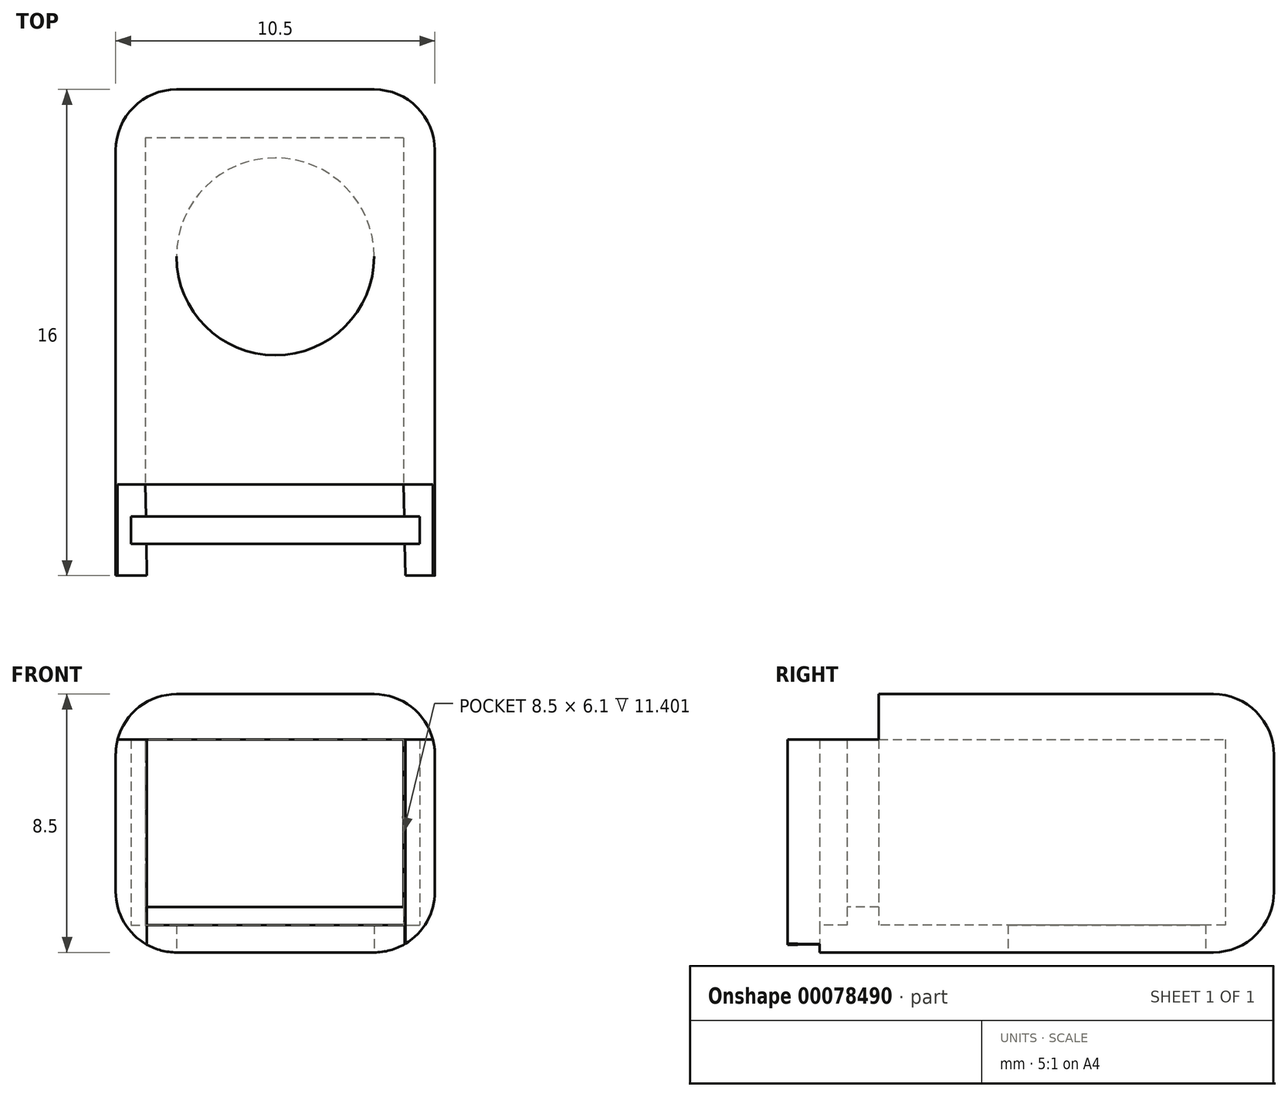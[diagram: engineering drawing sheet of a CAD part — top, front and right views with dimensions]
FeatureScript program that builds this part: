
annotation { "Feature Type Name" : "Feature", "Feature Type Description" : "" }
export const myFeature = defineFeature(function(context is Context, id is Id, definition is map)
    precondition{}
    {
        {
            var Q0;
            Q0=qCreatedBy(makeId("Top.planeOp"),FACE);
            var sketch = newSketch(context, id + "F0", { "sketchPlane" : qUnion([Q0])});
            skPoint(sketch, "E0.rect.middle", {"position": v(0, 0) * mm});
            skLineSegment(sketch, "E1.rect.bottom", {"start": v(-5.25, -1.5) * mm, "end": v(5.25, -1.5) * mm});
            skLineSegment(sketch, "E1.rect.top", {"start": v(-5.25, 1.5) * mm, "end": v(-4.28, 1.5) * mm});
            skLineSegment(sketch, "E1.rect.left", {"start": v(-5.25, -1.5) * mm, "end": v(-5.25, 1.5) * mm});
            skLineSegment(sketch, "E1.rect.right", {"start": v(5.25, -1.5) * mm, "end": v(5.25, 1.5) * mm});
            skLineSegment(sketch, "E2.rect.bottom", {"start": v(4.75, -0.45) * mm, "end": v(-4.75, -0.45) * mm});
            skLineSegment(sketch, "E2.rect.top", {"start": v(4.75, 0.45) * mm, "end": v(-4.75, 0.45) * mm});
            skLineSegment(sketch, "E2.rect.left", {"start": v(4.75, -0.45) * mm, "end": v(4.75, 0.45) * mm});
            skLineSegment(sketch, "E2.rect.right", {"start": v(-4.75, -0.45) * mm, "end": v(-4.75, 0.45) * mm});
            skLineSegment(sketch, "E3.rect.bottom", {"start": v(-4.22, -1.5) * mm, "end": v(4.28, -1.5) * mm});
            skLineSegment(sketch, "E3.rect.left", {"start": v(-4.22, -1.5) * mm, "end": v(-4.28, 1.5) * mm});
            skLineSegment(sketch, "E3.rect.right", {"start": v(4.28, -1.5) * mm, "end": v(4.22, 1.5) * mm});
            skLineSegment(sketch, "E4.trimOffspring", {"start": v(4.22, 1.5) * mm, "end": v(5.25, 1.5) * mm});
            skLineSegment(sketch, "E5", {"start": v(-4.28, 1.5) * mm, "end": v(4.22, 1.5) * mm, "construction": true});
            skLineSegment(sketch, "E6.bottom", {"start": v(5.25, 1.5) * mm, "end": v(-5.25, 1.5) * mm});
            skLineSegment(sketch, "E7.bottom", {"start": v(4.22, 1.5) * mm, "end": v(-5.25, 1.5) * mm});
            skLineSegment(sketch, "E8.bottom", {"start": v(-5.25, 1.5) * mm, "end": v(5.25, 1.5) * mm});
            skLineSegment(sketch, "E8.top", {"start": v(-5.25, 14.5) * mm, "end": v(5.25, 14.5) * mm});
            skLineSegment(sketch, "E8.left", {"start": v(-5.25, 1.5) * mm, "end": v(-5.25, 14.5) * mm});
            skLineSegment(sketch, "E8.right", {"start": v(5.25, 1.5) * mm, "end": v(5.25, 14.5) * mm});
            skLineSegment(sketch, "E9", {"start": v(-4.28, 1.5) * mm, "end": v(-4.28, 14.5) * mm});
            skLineSegment(sketch, "E10", {"start": v(4.22, 1.5) * mm, "end": v(4.22, 14.5) * mm});
            skLineSegment(sketch, "E11", {"start": v(-5.25, 12.9) * mm, "end": v(5.25, 12.9) * mm});
            skSolve(sketch);
        }
        {
            var Q0;
            {var subQ0=sQuery(id+"F0.wireOp",EDGE,"E6.right");Q0=makeQuery(id+"F0.imprint","IMPRINT",FACE,{"disambiguationData":[TD([[makeQuery(id+"F0.imprint","IMPRINT",EDGE,{"derivedFrom":subQ0}),-1.0]])]});}
            var Q1;
            Q1=makeQuery(id+"F0.imprint","IMPRINT",FACE,{"disambiguationData":[TD([[makeQuery(id+"F0.imprint","IMPRINT",EDGE,{"derivedFrom":sQuery(id+"F0.wireOp",EDGE,"E7.bottom")}),-1.0]])]});
            var Q2;
            {var subQ5=sQuery(id+"F0.wireOp",EDGE,"E7.bottom");Q2=makeQuery(id+"F0.imprint","IMPRINT",FACE,{"disambiguationData":[TD([[makeQuery(id+"F0.imprint","IMPRINT",EDGE,{"derivedFrom":subQ5}),1.0]])]});}
            var Q3;
            {var subQ8=sQuery(id+"F0.wireOp",EDGE,"E1.rect.right");Q3=makeQuery(id+"F0.imprint","IMPRINT",FACE,{"disambiguationData":[TD([[makeQuery(id+"F0.imprint","IMPRINT",EDGE,{"derivedFrom":subQ8}),1.0]])]});}
            var Q4;
            {var subQ5=sQuery(id+"F0.wireOp",EDGE,"E3.rect.bottom");Q4=makeQuery(id+"F0.imprint","IMPRINT",FACE,{"disambiguationData":[TD([[makeQuery(id+"F0.imprint","IMPRINT",EDGE,{"derivedFrom":subQ5}),1.0]])]});}
            var Q5;
            {var subQ4=sQuery(id+"F0.wireOp",EDGE,"E1.rect.left");Q5=makeQuery(id+"F0.imprint","IMPRINT",FACE,{"disambiguationData":[TD([[makeQuery(id+"F0.imprint","IMPRINT",EDGE,{"derivedFrom":subQ4}),-1.0]])]});}
            var Q6;
            {var subQ0=sQuery(id+"F0.wireOp",EDGE,"E6.left");Q6=makeQuery(id+"F0.imprint","IMPRINT",FACE,{"disambiguationData":[TD([[makeQuery(id+"F0.imprint","IMPRINT",EDGE,{"derivedFrom":subQ0}),1.0]])]});}
            var Q7;
            {var subQ0=sQuery(id+"F0.wireOp",EDGE,"E3.rect.right");var subQ1=sQuery(id+"F0.wireOp",EDGE,"E2.rect.bottom");var subQ2=makeQuery(id+"F0.imprint","INTERSECT",VERTEX,{"derivedFrom":[subQ1,subQ0]});Q7=makeQuery(id+"F0.imprint","IMPRINT",FACE,{"disambiguationData":[TD([[makeQuery(id+"F0.imprint","IMPRINT",EDGE,{"disambiguationData":[TD([[subQ2,-1.0]])],"derivedFrom":subQ1}),-1.0]])]});}
            var Q8;
            {var subQ0=sQuery(id+"F0.wireOp",EDGE,"E2.rect.right");Q8=makeQuery(id+"F0.imprint","IMPRINT",FACE,{"disambiguationData":[TD([[makeQuery(id+"F0.imprint","IMPRINT",EDGE,{"derivedFrom":subQ0}),-1.0]])]});}
            var Q9;
            {var subQ0=sQuery(id+"F0.wireOp",EDGE,"E2.rect.left");Q9=makeQuery(id+"F0.imprint","IMPRINT",FACE,{"disambiguationData":[TD([[makeQuery(id+"F0.imprint","IMPRINT",EDGE,{"derivedFrom":subQ0}),1.0]])]});}
            var Q10;
            {var subQ0=sQuery(id+"F0.wireOp",EDGE,"E8.left");var subQ5=sQuery(id+"F0.wireOp",EDGE,"GkOf4P8d-EZpd-A0Uh-Zg2V-Pxibx59UNKdc");var subQ6=makeQuery(id+"F0.imprint","INTERSECT",VERTEX,{"derivedFrom":[subQ0,subQ5]});Q10=makeQuery(id+"F0.imprint","IMPRINT",FACE,{"disambiguationData":[TD([[makeQuery(id+"F0.imprint","IMPRINT",EDGE,{"disambiguationData":[TD([[subQ6,1.0]])],"derivedFrom":subQ5}),1.0]])]});}
            var Q11;
            {var subQ0=sQuery(id+"F0.wireOp",EDGE,"E8.left");var subQ1=sQuery(id+"F0.wireOp",EDGE,"E8.top");var subQ2=makeQuery(id+"F0.imprint","INTERSECT",VERTEX,{"derivedFrom":[subQ1,subQ0]});Q11=makeQuery(id+"F0.imprint","IMPRINT",FACE,{"disambiguationData":[TD([[makeQuery(id+"F0.imprint","IMPRINT",EDGE,{"disambiguationData":[TD([[subQ2,-1.0]])],"derivedFrom":subQ1}),-1.0]])]});}
            var Q12;
            {var subQ0=sQuery(id+"F0.wireOp",EDGE,"E9");var subQ1=sQuery(id+"F0.wireOp",EDGE,"E8.top");var subQ2=makeQuery(id+"F0.imprint","INTERSECT",VERTEX,{"derivedFrom":[subQ1,subQ0]});Q12=makeQuery(id+"F0.imprint","IMPRINT",FACE,{"disambiguationData":[TD([[makeQuery(id+"F0.imprint","IMPRINT",EDGE,{"disambiguationData":[TD([[subQ2,-1.0]])],"derivedFrom":subQ1}),-1.0]])]});}
            var Q13;
            {var subQ0=sQuery(id+"F0.wireOp",EDGE,"E8.right");var subQ1=sQuery(id+"F0.wireOp",EDGE,"E8.top");var subQ2=makeQuery(id+"F0.imprint","INTERSECT",VERTEX,{"derivedFrom":[subQ1,subQ0]});Q13=makeQuery(id+"F0.imprint","IMPRINT",FACE,{"disambiguationData":[TD([[makeQuery(id+"F0.imprint","IMPRINT",EDGE,{"disambiguationData":[TD([[subQ2,1.0]])],"derivedFrom":subQ1}),-1.0]])]});}
            var Q14;
            {var subQ0=sQuery(id+"F0.wireOp",EDGE,"E8.right");var subQ5=sQuery(id+"F0.wireOp",EDGE,"GkOf4P8d-EZpd-A0Uh-Zg2V-Pxibx59UNKdc");var subQ6=makeQuery(id+"F0.imprint","INTERSECT",VERTEX,{"derivedFrom":[subQ0,subQ5]});Q14=makeQuery(id+"F0.imprint","IMPRINT",FACE,{"disambiguationData":[TD([[makeQuery(id+"F0.imprint","IMPRINT",EDGE,{"disambiguationData":[TD([[subQ6,-1.0]])],"derivedFrom":subQ5}),1.0]])]});}
            var Q15;
            {var subQ0=sQuery(id+"F0.wireOp",EDGE,"E3.rect.right");var subQ1=sQuery(id+"F0.wireOp",EDGE,"E2.rect.top");var subQ2=makeQuery(id+"F0.imprint","INTERSECT",VERTEX,{"derivedFrom":[subQ1,subQ0]});Q15=makeQuery(id+"F0.imprint","IMPRINT",FACE,{"disambiguationData":[TD([[makeQuery(id+"F0.imprint","IMPRINT",EDGE,{"disambiguationData":[TD([[subQ2,-1.0]])],"derivedFrom":subQ1}),-1.0]])]});}
            var Q16;
            {var subQ0=sQuery(id+"F0.wireOp",EDGE,"E9");var subQ5=sQuery(id+"F0.wireOp",EDGE,"GkOf4P8d-EZpd-A0Uh-Zg2V-Pxibx59UNKdc");var subQ6=makeQuery(id+"F0.imprint","INTERSECT",VERTEX,{"derivedFrom":[subQ0,subQ5]});Q16=makeQuery(id+"F0.imprint","IMPRINT",FACE,{"disambiguationData":[TD([[makeQuery(id+"F0.imprint","IMPRINT",EDGE,{"disambiguationData":[TD([[subQ6,1.0]])],"derivedFrom":subQ5}),1.0]])]});}
            var Q17;
            {var subQ0=sQuery(id+"F0.wireOp",EDGE,"E8.left");var subQ5=sQuery(id+"F0.wireOp",EDGE,"E11");var subQ6=makeQuery(id+"F0.imprint","INTERSECT",VERTEX,{"derivedFrom":[subQ0,subQ5]});Q17=makeQuery(id+"F0.imprint","IMPRINT",FACE,{"disambiguationData":[TD([[makeQuery(id+"F0.imprint","IMPRINT",EDGE,{"disambiguationData":[TD([[subQ6,-1.0]])],"derivedFrom":subQ5}),-1.0]])]});}
            var Q18;
            {var subQ0=sQuery(id+"F0.wireOp",EDGE,"E9");var subQ5=sQuery(id+"F0.wireOp",EDGE,"E11");var subQ6=makeQuery(id+"F0.imprint","INTERSECT",VERTEX,{"derivedFrom":[subQ0,subQ5]});Q18=makeQuery(id+"F0.imprint","IMPRINT",FACE,{"disambiguationData":[TD([[makeQuery(id+"F0.imprint","IMPRINT",EDGE,{"disambiguationData":[TD([[subQ6,-1.0]])],"derivedFrom":subQ5}),-1.0]])]});}
            var Q19;
            {var subQ0=sQuery(id+"F0.wireOp",EDGE,"E8.right");var subQ5=sQuery(id+"F0.wireOp",EDGE,"E11");var subQ6=makeQuery(id+"F0.imprint","INTERSECT",VERTEX,{"derivedFrom":[subQ0,subQ5]});Q19=makeQuery(id+"F0.imprint","IMPRINT",FACE,{"disambiguationData":[TD([[makeQuery(id+"F0.imprint","IMPRINT",EDGE,{"disambiguationData":[TD([[subQ6,1.0]])],"derivedFrom":subQ5}),-1.0]])]});}
            extrude(context, id + "F1", {"entities" : qUnion([Q0, Q1, Q2, Q3, Q4, Q5, Q6, Q7, Q8, Q9, Q10, Q11, Q12, Q13, Q14, Q15, Q16, Q17, Q18, Q19]), "depth" : 0.9 * mm});
        }
        {
            var Q0;
            {var subQ0=sQuery(id+"F0.wireOp",EDGE,"E6.left");Q0=makeQuery(id+"F0.imprint","IMPRINT",FACE,{"disambiguationData":[TD([[makeQuery(id+"F0.imprint","IMPRINT",EDGE,{"derivedFrom":subQ0}),1.0]])]});}
            var Q1;
            {var subQ0=sQuery(id+"F0.wireOp",EDGE,"E6.right");Q1=makeQuery(id+"F0.imprint","IMPRINT",FACE,{"disambiguationData":[TD([[makeQuery(id+"F0.imprint","IMPRINT",EDGE,{"derivedFrom":subQ0}),-1.0]])]});}
            var Q2;
            {var subQ5=sQuery(id+"F0.wireOp",EDGE,"E3.rect.bottom");Q2=makeQuery(id+"F0.imprint","IMPRINT",FACE,{"disambiguationData":[TD([[makeQuery(id+"F0.imprint","IMPRINT",EDGE,{"derivedFrom":subQ5}),1.0]])]});}
            var Q3;
            {var subQ4=sQuery(id+"F0.wireOp",EDGE,"E1.rect.left");Q3=makeQuery(id+"F0.imprint","IMPRINT",FACE,{"disambiguationData":[TD([[makeQuery(id+"F0.imprint","IMPRINT",EDGE,{"derivedFrom":subQ4}),-1.0]])]});}
            var Q4;
            {var subQ8=sQuery(id+"F0.wireOp",EDGE,"E1.rect.right");Q4=makeQuery(id+"F0.imprint","IMPRINT",FACE,{"disambiguationData":[TD([[makeQuery(id+"F0.imprint","IMPRINT",EDGE,{"derivedFrom":subQ8}),1.0]])]});}
            var Q5;
            {var subQ5=sQuery(id+"F0.wireOp",EDGE,"E7.bottom");Q5=makeQuery(id+"F0.imprint","IMPRINT",FACE,{"disambiguationData":[TD([[makeQuery(id+"F0.imprint","IMPRINT",EDGE,{"derivedFrom":subQ5}),1.0]])]});}
            var Q6;
            {var subQ0=sQuery(id+"F0.wireOp",EDGE,"E8.right");var subQ5=sQuery(id+"F0.wireOp",EDGE,"GkOf4P8d-EZpd-A0Uh-Zg2V-Pxibx59UNKdc");var subQ6=makeQuery(id+"F0.imprint","INTERSECT",VERTEX,{"derivedFrom":[subQ0,subQ5]});Q6=makeQuery(id+"F0.imprint","IMPRINT",FACE,{"disambiguationData":[TD([[makeQuery(id+"F0.imprint","IMPRINT",EDGE,{"disambiguationData":[TD([[subQ6,-1.0]])],"derivedFrom":subQ5}),1.0]])]});}
            var Q7;
            {var subQ0=sQuery(id+"F0.wireOp",EDGE,"E3.rect.right");var subQ1=sQuery(id+"F0.wireOp",EDGE,"E2.rect.top");var subQ2=makeQuery(id+"F0.imprint","INTERSECT",VERTEX,{"derivedFrom":[subQ1,subQ0]});Q7=makeQuery(id+"F0.imprint","IMPRINT",FACE,{"disambiguationData":[TD([[makeQuery(id+"F0.imprint","IMPRINT",EDGE,{"disambiguationData":[TD([[subQ2,-1.0]])],"derivedFrom":subQ1}),-1.0]])]});}
            var Q8;
            {var subQ0=sQuery(id+"F0.wireOp",EDGE,"E9");var subQ5=sQuery(id+"F0.wireOp",EDGE,"GkOf4P8d-EZpd-A0Uh-Zg2V-Pxibx59UNKdc");var subQ6=makeQuery(id+"F0.imprint","INTERSECT",VERTEX,{"derivedFrom":[subQ0,subQ5]});Q8=makeQuery(id+"F0.imprint","IMPRINT",FACE,{"disambiguationData":[TD([[makeQuery(id+"F0.imprint","IMPRINT",EDGE,{"disambiguationData":[TD([[subQ6,1.0]])],"derivedFrom":subQ5}),1.0]])]});}
            var Q9;
            {var subQ0=sQuery(id+"F0.wireOp",EDGE,"E8.left");var subQ5=sQuery(id+"F0.wireOp",EDGE,"GkOf4P8d-EZpd-A0Uh-Zg2V-Pxibx59UNKdc");var subQ6=makeQuery(id+"F0.imprint","INTERSECT",VERTEX,{"derivedFrom":[subQ0,subQ5]});Q9=makeQuery(id+"F0.imprint","IMPRINT",FACE,{"disambiguationData":[TD([[makeQuery(id+"F0.imprint","IMPRINT",EDGE,{"disambiguationData":[TD([[subQ6,1.0]])],"derivedFrom":subQ5}),1.0]])]});}
            var Q10;
            {var subQ0=sQuery(id+"F0.wireOp",EDGE,"E8.left");var subQ1=sQuery(id+"F0.wireOp",EDGE,"E8.top");var subQ2=makeQuery(id+"F0.imprint","INTERSECT",VERTEX,{"derivedFrom":[subQ1,subQ0]});Q10=makeQuery(id+"F0.imprint","IMPRINT",FACE,{"disambiguationData":[TD([[makeQuery(id+"F0.imprint","IMPRINT",EDGE,{"disambiguationData":[TD([[subQ2,-1.0]])],"derivedFrom":subQ1}),-1.0]])]});}
            var Q11;
            {var subQ0=sQuery(id+"F0.wireOp",EDGE,"E9");var subQ1=sQuery(id+"F0.wireOp",EDGE,"E8.top");var subQ2=makeQuery(id+"F0.imprint","INTERSECT",VERTEX,{"derivedFrom":[subQ1,subQ0]});Q11=makeQuery(id+"F0.imprint","IMPRINT",FACE,{"disambiguationData":[TD([[makeQuery(id+"F0.imprint","IMPRINT",EDGE,{"disambiguationData":[TD([[subQ2,-1.0]])],"derivedFrom":subQ1}),-1.0]])]});}
            var Q12;
            {var subQ0=sQuery(id+"F0.wireOp",EDGE,"E8.right");var subQ1=sQuery(id+"F0.wireOp",EDGE,"E8.top");var subQ2=makeQuery(id+"F0.imprint","INTERSECT",VERTEX,{"derivedFrom":[subQ1,subQ0]});Q12=makeQuery(id+"F0.imprint","IMPRINT",FACE,{"disambiguationData":[TD([[makeQuery(id+"F0.imprint","IMPRINT",EDGE,{"disambiguationData":[TD([[subQ2,1.0]])],"derivedFrom":subQ1}),-1.0]])]});}
            var Q13;
            {var subQ0=sQuery(id+"F0.wireOp",EDGE,"E8.left");var subQ5=sQuery(id+"F0.wireOp",EDGE,"E11");var subQ6=makeQuery(id+"F0.imprint","INTERSECT",VERTEX,{"derivedFrom":[subQ0,subQ5]});Q13=makeQuery(id+"F0.imprint","IMPRINT",FACE,{"disambiguationData":[TD([[makeQuery(id+"F0.imprint","IMPRINT",EDGE,{"disambiguationData":[TD([[subQ6,-1.0]])],"derivedFrom":subQ5}),-1.0]])]});}
            var Q14;
            {var subQ0=sQuery(id+"F0.wireOp",EDGE,"E8.right");var subQ5=sQuery(id+"F0.wireOp",EDGE,"E11");var subQ6=makeQuery(id+"F0.imprint","INTERSECT",VERTEX,{"derivedFrom":[subQ0,subQ5]});Q14=makeQuery(id+"F0.imprint","IMPRINT",FACE,{"disambiguationData":[TD([[makeQuery(id+"F0.imprint","IMPRINT",EDGE,{"disambiguationData":[TD([[subQ6,1.0]])],"derivedFrom":subQ5}),-1.0]])]});}
            extrude(context, id + "F2", {"entities" : qUnion([Q0, Q1, Q2, Q3, Q4, Q5, Q6, Q7, Q8, Q9, Q10, Q11, Q12, Q13, Q14]), "operationType" : NewBodyOperationType.ADD, "depth" : 1.5 * mm});
        }
        {
            var Q0;
            {var subQ9=sQuery(id+"F0.wireOp",EDGE,"E1.rect.top");Q0=makeQuery(id+"F0.imprint","IMPRINT",FACE,{"disambiguationData":[TD([[makeQuery(id+"F0.imprint","IMPRINT",EDGE,{"derivedFrom":subQ9}),-1.0]])]});}
            var Q1;
            {var subQ4=sQuery(id+"F0.wireOp",EDGE,"E1.rect.right");Q1=makeQuery(id+"F0.imprint","IMPRINT",FACE,{"disambiguationData":[TD([[makeQuery(id+"F0.imprint","IMPRINT",EDGE,{"derivedFrom":subQ4}),1.0]])]});}
            var Q2;
            {var subQ4=sQuery(id+"F0.wireOp",EDGE,"E1.rect.left");Q2=makeQuery(id+"F0.imprint","IMPRINT",FACE,{"disambiguationData":[TD([[makeQuery(id+"F0.imprint","IMPRINT",EDGE,{"derivedFrom":subQ4}),-1.0]])]});}
            var Q3;
            {var subQ0=sQuery(id+"F0.wireOp",EDGE,"E6.right");Q3=makeQuery(id+"F0.imprint","IMPRINT",FACE,{"disambiguationData":[TD([[makeQuery(id+"F0.imprint","IMPRINT",EDGE,{"derivedFrom":subQ0}),-1.0]])]});}
            var Q4;
            {var subQ0=sQuery(id+"F0.wireOp",EDGE,"E6.left");Q4=makeQuery(id+"F0.imprint","IMPRINT",FACE,{"disambiguationData":[TD([[makeQuery(id+"F0.imprint","IMPRINT",EDGE,{"derivedFrom":subQ0}),1.0]])]});}
            var Q5;
            {var subQ0=sQuery(id+"F0.wireOp",EDGE,"E8.left");var subQ5=sQuery(id+"F0.wireOp",EDGE,"GkOf4P8d-EZpd-A0Uh-Zg2V-Pxibx59UNKdc");var subQ6=makeQuery(id+"F0.imprint","INTERSECT",VERTEX,{"derivedFrom":[subQ0,subQ5]});Q5=makeQuery(id+"F0.imprint","IMPRINT",FACE,{"disambiguationData":[TD([[makeQuery(id+"F0.imprint","IMPRINT",EDGE,{"disambiguationData":[TD([[subQ6,1.0]])],"derivedFrom":subQ5}),1.0]])]});}
            var Q6;
            {var subQ0=sQuery(id+"F0.wireOp",EDGE,"E8.right");var subQ5=sQuery(id+"F0.wireOp",EDGE,"GkOf4P8d-EZpd-A0Uh-Zg2V-Pxibx59UNKdc");var subQ6=makeQuery(id+"F0.imprint","INTERSECT",VERTEX,{"derivedFrom":[subQ0,subQ5]});Q6=makeQuery(id+"F0.imprint","IMPRINT",FACE,{"disambiguationData":[TD([[makeQuery(id+"F0.imprint","IMPRINT",EDGE,{"disambiguationData":[TD([[subQ6,-1.0]])],"derivedFrom":subQ5}),1.0]])]});}
            var Q7;
            {var subQ0=sQuery(id+"F0.wireOp",EDGE,"E8.left");var subQ1=sQuery(id+"F0.wireOp",EDGE,"E8.top");var subQ2=makeQuery(id+"F0.imprint","INTERSECT",VERTEX,{"derivedFrom":[subQ1,subQ0]});Q7=makeQuery(id+"F0.imprint","IMPRINT",FACE,{"disambiguationData":[TD([[makeQuery(id+"F0.imprint","IMPRINT",EDGE,{"disambiguationData":[TD([[subQ2,-1.0]])],"derivedFrom":subQ1}),-1.0]])]});}
            var Q8;
            {var subQ0=sQuery(id+"F0.wireOp",EDGE,"E9");var subQ1=sQuery(id+"F0.wireOp",EDGE,"E8.top");var subQ2=makeQuery(id+"F0.imprint","INTERSECT",VERTEX,{"derivedFrom":[subQ1,subQ0]});Q8=makeQuery(id+"F0.imprint","IMPRINT",FACE,{"disambiguationData":[TD([[makeQuery(id+"F0.imprint","IMPRINT",EDGE,{"disambiguationData":[TD([[subQ2,-1.0]])],"derivedFrom":subQ1}),-1.0]])]});}
            var Q9;
            {var subQ0=sQuery(id+"F0.wireOp",EDGE,"E8.right");var subQ1=sQuery(id+"F0.wireOp",EDGE,"E8.top");var subQ2=makeQuery(id+"F0.imprint","INTERSECT",VERTEX,{"derivedFrom":[subQ1,subQ0]});Q9=makeQuery(id+"F0.imprint","IMPRINT",FACE,{"disambiguationData":[TD([[makeQuery(id+"F0.imprint","IMPRINT",EDGE,{"disambiguationData":[TD([[subQ2,1.0]])],"derivedFrom":subQ1}),-1.0]])]});}
            var Q10;
            {var subQ0=sQuery(id+"F0.wireOp",EDGE,"E8.left");var subQ5=sQuery(id+"F0.wireOp",EDGE,"E11");var subQ6=makeQuery(id+"F0.imprint","INTERSECT",VERTEX,{"derivedFrom":[subQ0,subQ5]});Q10=makeQuery(id+"F0.imprint","IMPRINT",FACE,{"disambiguationData":[TD([[makeQuery(id+"F0.imprint","IMPRINT",EDGE,{"disambiguationData":[TD([[subQ6,-1.0]])],"derivedFrom":subQ5}),-1.0]])]});}
            var Q11;
            {var subQ0=sQuery(id+"F0.wireOp",EDGE,"E8.right");var subQ5=sQuery(id+"F0.wireOp",EDGE,"E11");var subQ6=makeQuery(id+"F0.imprint","INTERSECT",VERTEX,{"derivedFrom":[subQ0,subQ5]});Q11=makeQuery(id+"F0.imprint","IMPRINT",FACE,{"disambiguationData":[TD([[makeQuery(id+"F0.imprint","IMPRINT",EDGE,{"disambiguationData":[TD([[subQ6,1.0]])],"derivedFrom":subQ5}),-1.0]])]});}
            extrude(context, id + "F3", {"entities" : qUnion([Q0, Q1, Q2, Q3, Q4, Q5, Q6, Q7, Q8, Q9, Q10, Q11]), "operationType" : NewBodyOperationType.ADD, "depth" : 7 * mm});
        }
        {
            var Q0;
            Q0=makeQuery(id+"F3.opExtrude","CAP_FACE",FACE,{"disambiguationData":[OSD([sQuery(id+"F0.wireOp",EDGE,"E1.rect.bottom"),sQuery(id+"F0.wireOp",EDGE,"E1.rect.left"),sQuery(id+"F0.wireOp",EDGE,"E1.rect.right"),sQuery(id+"F0.wireOp",EDGE,"E2.rect.bottom"),sQuery(id+"F0.wireOp",EDGE,"E2.rect.top"),sQuery(id+"F0.wireOp",EDGE,"E2.rect.left"),sQuery(id+"F0.wireOp",EDGE,"E2.rect.right"),sQuery(id+"F0.wireOp",EDGE,"E3.rect.left"),sQuery(id+"F0.wireOp",EDGE,"E3.rect.right"),sQuery(id+"F0.wireOp",EDGE,"E8.top"),sQuery(id+"F0.wireOp",EDGE,"E8.left"),sQuery(id+"F0.wireOp",EDGE,"E8.right"),sQuery(id+"F0.wireOp",EDGE,"E9"),sQuery(id+"F0.wireOp",EDGE,"E10"),sQuery(id+"F0.wireOp",EDGE,"GkOf4P8d-EZpd-A0Uh-Zg2V-Pxibx59UNKdc")])],"isStart":false});
            cPlane(context, id + "F4", {"entities" : qUnion([Q0]), "cplaneType" : CPlaneType.OFFSET, "offset" : 0 * mm, "width" : 150 * mm, "height" : 150 * mm});
        }
        {
            var Q0;
            Q0=qCreatedBy(id+"F4.planeOp",FACE);
            var sketch = newSketch(context, id + "F5", { "sketchPlane" : qUnion([Q0])});
            skLineSegment(sketch, "E12.bottom", {"start": v(5.25, 1.5) * mm, "end": v(-5.25, 1.5) * mm});
            skLineSegment(sketch, "E12.top", {"start": v(5.25, -1.5) * mm, "end": v(-5.25, -1.5) * mm});
            skLineSegment(sketch, "E12.left", {"start": v(5.25, 1.5) * mm, "end": v(5.25, -1.5) * mm});
            skLineSegment(sketch, "E12.right", {"start": v(-5.25, 1.5) * mm, "end": v(-5.25, -1.5) * mm});
            skPoint(sketch, "E12.middle", {"position": v(0, 0) * mm});
            skLineSegment(sketch, "E13.top", {"start": v(5.25, 14.5) * mm, "end": v(-5.25, 14.5) * mm});
            skLineSegment(sketch, "E13.left", {"start": v(5.25, 1.5) * mm, "end": v(5.25, 14.5) * mm});
            skLineSegment(sketch, "E13.right", {"start": v(-5.25, 1.5) * mm, "end": v(-5.25, 14.5) * mm});
            skSolve(sketch);
        }
        {
            var Q0;
            Q0=makeQuery(id+"F5.imprint","IMPRINT",FACE,{"disambiguationData":[TD([[makeQuery(id+"F5.imprint","IMPRINT",EDGE,{"derivedFrom":sQuery(id+"F5.wireOp",EDGE,"E12.bottom")}),-1.0]])]});
            extrude(context, id + "F6", {"entities" : qUnion([Q0]), "operationType" : NewBodyOperationType.ADD, "depth" : 1.5 * mm});
        }
        {
            var Q0;
            {var subQ0=sQuery(id+"F0.wireOp",EDGE,"E8.right");var subQ1=sQuery(id+"F0.wireOp",EDGE,"E8.top");Q0=makeQuery(id+"F6.boolean.opBoolean","MERGE",EDGE,{"derivedFrom":[makeQuery(id+"F3.boolean.opBoolean","MERGE",EDGE,{"derivedFrom":[makeQuery(id+"F2.boolean.opBoolean","MERGE",EDGE,{"derivedFrom":[makeQuery(id+"F1.opExtrude","SWEPT_EDGE",EDGE,{"disambiguationData":[OSD([subQ1,subQ0])]}),makeQuery(id+"F2.opExtrude","SWEPT_EDGE",EDGE,{"disambiguationData":[OSD([subQ1,subQ0])]})]}),makeQuery(id+"F3.opExtrude","SWEPT_EDGE",EDGE,{"disambiguationData":[OSD([subQ1,subQ0])]})]}),makeQuery(id+"F6.opExtrude","SWEPT_EDGE",EDGE,{"disambiguationData":[OSD([sQuery(id+"F5.wireOp",EDGE,"E13.top"),sQuery(id+"F5.wireOp",EDGE,"E13.left")])]})]});}
            var Q1;
            Q1=makeQuery(id+"F6.opExtrude","CAP_EDGE",EDGE,{"disambiguationData":[OSD([sQuery(id+"F5.wireOp",EDGE,"E13.top")])],"isStart":false});
            var Q2;
            Q2=makeQuery(id+"F6.opExtrude","CAP_EDGE",EDGE,{"disambiguationData":[OSD([sQuery(id+"F5.wireOp",EDGE,"E13.left")])],"isStart":false});
            var Q3;
            Q3=makeQuery(id+"F1.opExtrude","CAP_EDGE",EDGE,{"disambiguationData":[OSD([sQuery(id+"F0.wireOp",EDGE,"E1.rect.right"),sQuery(id+"F0.wireOp",EDGE,"E8.right")])],"isStart":true});
            var Q4;
            Q4=makeQuery(id+"F1.opExtrude","CAP_EDGE",EDGE,{"disambiguationData":[OSD([sQuery(id+"F0.wireOp",EDGE,"E8.top")])],"isStart":true});
            var Q5;
            Q5=makeQuery(id+"F1.opExtrude","CAP_EDGE",EDGE,{"disambiguationData":[OSD([sQuery(id+"F0.wireOp",EDGE,"E1.rect.left"),sQuery(id+"F0.wireOp",EDGE,"E8.left")])],"isStart":true});
            var Q6;
            {var subQ0=sQuery(id+"F0.wireOp",EDGE,"E8.left");var subQ1=sQuery(id+"F0.wireOp",EDGE,"E8.top");Q6=makeQuery(id+"F6.boolean.opBoolean","MERGE",EDGE,{"derivedFrom":[makeQuery(id+"F3.boolean.opBoolean","MERGE",EDGE,{"derivedFrom":[makeQuery(id+"F2.boolean.opBoolean","MERGE",EDGE,{"derivedFrom":[makeQuery(id+"F1.opExtrude","SWEPT_EDGE",EDGE,{"disambiguationData":[OSD([subQ1,subQ0])]}),makeQuery(id+"F2.opExtrude","SWEPT_EDGE",EDGE,{"disambiguationData":[OSD([subQ1,subQ0])]})]}),makeQuery(id+"F3.opExtrude","SWEPT_EDGE",EDGE,{"disambiguationData":[OSD([subQ1,subQ0])]})]}),makeQuery(id+"F6.opExtrude","SWEPT_EDGE",EDGE,{"disambiguationData":[OSD([sQuery(id+"F5.wireOp",EDGE,"E13.top"),sQuery(id+"F5.wireOp",EDGE,"E13.right")])]})]});}
            var Q7;
            Q7=makeQuery(id+"F6.opExtrude","CAP_EDGE",EDGE,{"disambiguationData":[OSD([sQuery(id+"F5.wireOp",EDGE,"E13.right")])],"isStart":false});
            fillet(context, id + "F7", {"entities" : qUnion([Q0, Q1, Q2, Q3, Q4, Q5, Q6, Q7]), "radius" : 2 * mm, "tangentPropagation" : true, "allowEdgeOverflow" : false});
        }
        {
            var Q0;
            Q0=qCreatedBy(makeId("Top.planeOp"),FACE);
            var sketch = newSketch(context, id + "F8", { "sketchPlane" : qUnion([Q0])});
            skLineSegment(sketch, "E14", {"start": v(0, 0) * mm, "end": v(0, 9) * mm});
            skCircle(sketch, "E15", {"center": v(0, 9) * mm, "radius": 3.25 * mm});
            skSolve(sketch);
        }
        {
            var Q0;
            Q0 = qSketchRegion(id + "F8", true);
            var Q1;
            Q1=makeQuery(id+"F1.opExtrude","CAP_FACE",FACE,{"disambiguationData":[OSD([sQuery(id+"F0.wireOp",EDGE,"E1.rect.bottom"),sQuery(id+"F0.wireOp",EDGE,"E1.rect.left"),sQuery(id+"F0.wireOp",EDGE,"E1.rect.right"),sQuery(id+"F0.wireOp",EDGE,"E3.rect.bottom"),sQuery(id+"F0.wireOp",EDGE,"E8.top"),sQuery(id+"F0.wireOp",EDGE,"E8.left"),sQuery(id+"F0.wireOp",EDGE,"E8.right")])],"isStart":true});
            extrude(context, id + "F9", {"entities" : qUnion([Q0]), "operationType" : NewBodyOperationType.REMOVE, "endBound" : BoundingType.UP_TO_NEXT, "endBoundEntityFace" : qUnion([Q1]), "depth" : 25 * mm});
        }
    });
